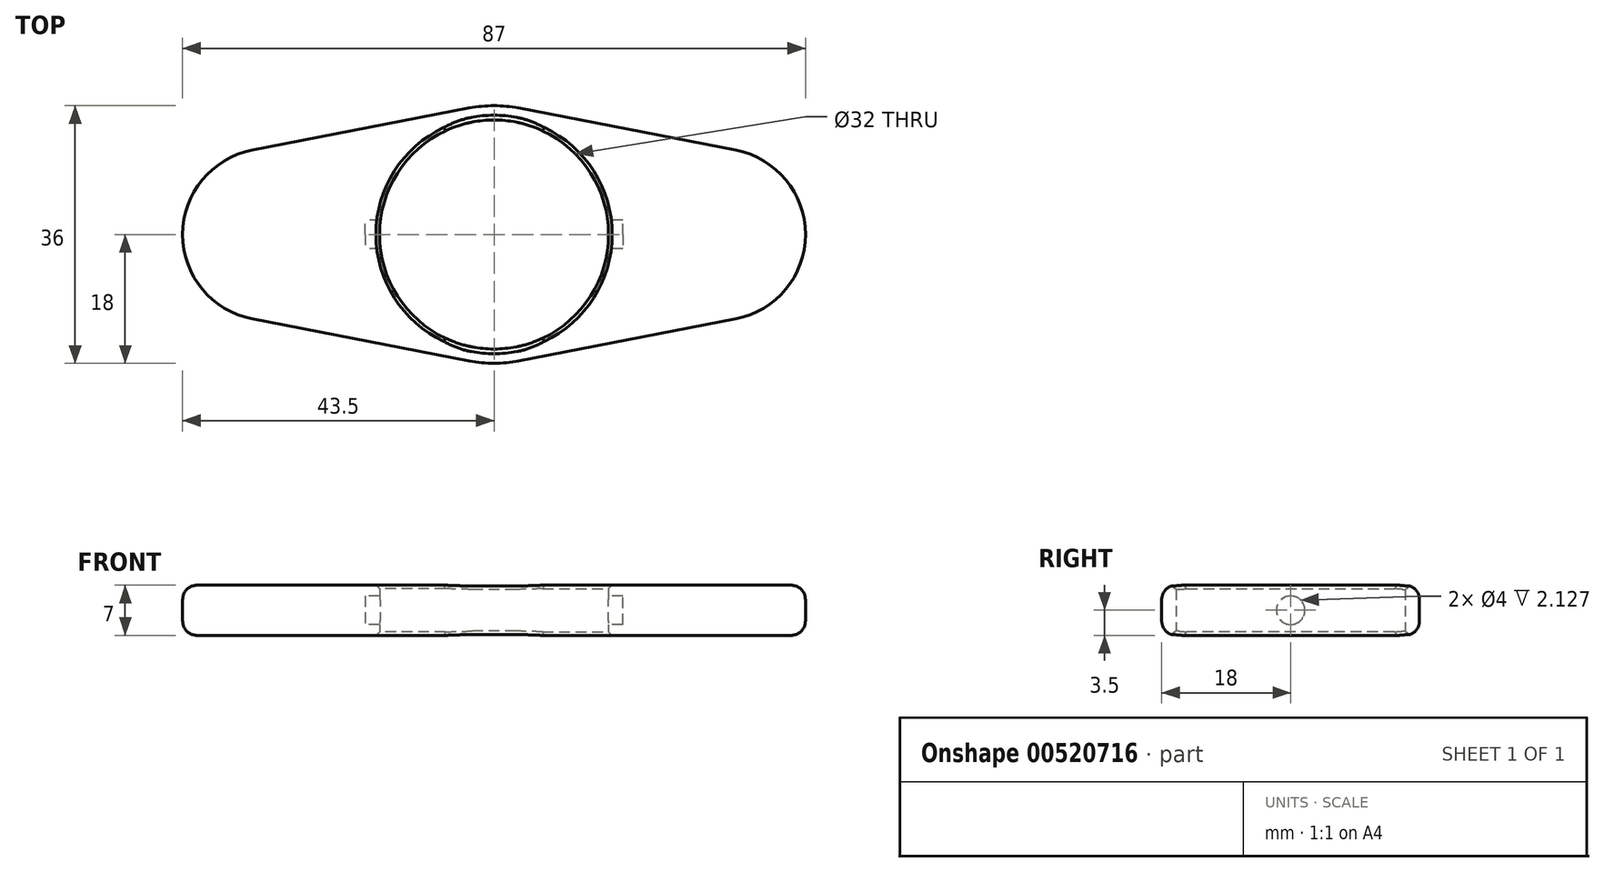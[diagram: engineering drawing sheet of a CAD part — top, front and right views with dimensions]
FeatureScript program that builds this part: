
annotation { "Feature Type Name" : "Feature", "Feature Type Description" : "" }
export const myFeature = defineFeature(function(context is Context, id is Id, definition is map)
    precondition{}
    {
        {
            var Q0;
            Q0=qCreatedBy(makeId("Top.planeOp"),FACE);
            var sketch = newSketch(context, id + "F0", { "sketchPlane" : qUnion([Q0])});
            skCircle(sketch, "E0", {"center": v(0, 0) * mm, "radius": 16 * mm});
            skArc(sketch, "E1", {"start": v(-3.43, -17.67) * mm, "mid": v(0, -18) * mm, "end": v(3.43, -17.67) * mm});
            skArc(sketch, "E2", {"start": v(33.79, -11.78) * mm, "mid": v(43.5, 0) * mm, "end": v(33.79, 11.78) * mm});
            skArc(sketch, "E3", {"start": v(-33.79, 11.78) * mm, "mid": v(-43.5, 0) * mm, "end": v(-33.79, -11.78) * mm});
            skLineSegment(sketch, "E4", {"start": v(-3.43, 17.67) * mm, "end": v(-33.79, 11.78) * mm});
            skLineSegment(sketch, "E5", {"start": v(-3.43, -17.67) * mm, "end": v(-33.79, -11.78) * mm});
            skLineSegment(sketch, "E6", {"start": v(3.43, 17.67) * mm, "end": v(33.79, 11.78) * mm});
            skLineSegment(sketch, "E7", {"start": v(33.79, -11.78) * mm, "end": v(3.43, -17.67) * mm});
            skArc(sketch, "E8.trimOffspring", {"start": v(3.43, 17.67) * mm, "mid": v(0, 18) * mm, "end": v(-3.43, 17.67) * mm});
            skCircle(sketch, "E9", {"center": v(0, 0) * mm, "radius": 43.5 * mm, "construction": true});
            skSolve(sketch);
        }
        {
            var Q0;
            Q0=makeQuery(id+"F0.imprint","IMPRINT",FACE,{"disambiguationData":[TD([[makeQuery(id+"F0.imprint","IMPRINT",EDGE,{"derivedFrom":sQuery(id+"F0.wireOp",EDGE,"E0")}),-1.0]])]});
            extrude(context, id + "F1", {"entities" : qUnion([Q0]), "depth" : 7 * mm});
        }
        {
            var Q0;
            Q0=makeQuery(id+"F1.opExtrude","CAP_EDGE",EDGE,{"disambiguationData":[OSD([sQuery(id+"F0.wireOp",EDGE,"E5")])],"isStart":false});
            var Q1;
            Q1=makeQuery(id+"F1.opExtrude","CAP_EDGE",EDGE,{"disambiguationData":[OSD([sQuery(id+"F0.wireOp",EDGE,"E5")])],"isStart":true});
            fillet(context, id + "F2", {"entities" : qUnion([Q0, Q1]), "radius" : 2 * mm, "tangentPropagation" : true, "allowEdgeOverflow" : false});
        }
        {
            var Q0;
            Q0=makeQuery(id+"F1.opExtrude","SWEPT_FACE",FACE,{"disambiguationData":[OSD([sQuery(id+"F0.wireOp",EDGE,"E0")])]});
            chamfer(context, id + "F3", {"entities" : qUnion([Q0]), "width" : .5 * mm, "tangentPropagation" : true});
        }
        {
            var Q0;
            Q0=qCreatedBy(makeId("Right.planeOp"),FACE);
            var sketch = newSketch(context, id + "F4", { "sketchPlane" : qUnion([Q0])});
            skCircle(sketch, "E10", {"center": v(0, 3.5) * mm, "radius": 2 * mm});
            skLineSegment(sketch, "E11", {"start": v(0, 7) * mm, "end": v(0, 3.5) * mm, "construction": true});
            skLineSegment(sketch, "E12", {"start": v(0, 3.5) * mm, "end": v(0, 0) * mm, "construction": true});
            skSolve(sketch);
        }
        {
            var Q0;
            Q0=qSketchRegion(id+"F4",true);
            extrude(context, id + "F5", {"entities" : qUnion([Q0]), "operationType" : NewBodyOperationType.REMOVE, "endBound" : BoundingType.SYMMETRIC, "depth" : 36 * mm});
        }
    });
